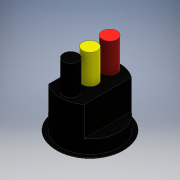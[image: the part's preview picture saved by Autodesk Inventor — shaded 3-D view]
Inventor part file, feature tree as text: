
AUTODESK INVENTOR PART (.ipt)
format: ipt  version: 2016 (Build 200138000, 138)  size: 154,112 bytes
history: native  units: mm
features: extrude x4, sketch x4, fillet x1, projected_geometry x1
ambient origin geometry x8: Origin, YZ Plane, XZ Plane, XY Plane, X Axis, Y Axis, Z Axis, Center Point
bodies: Solid1 (feature_tree)
feature tree (10):
  extrude  "Extrusion1"  Depth=4.5mm TaperAngle=0.0deg
  extrude  "Extrusion2"  Depth=10.0mm TaperAngle=0.0deg
  extrude  "Extrusion3"  Depth=1.0mm TaperAngle=0.0deg
  fillet  "Fillet1"  Radius=2.0mm
  extrude  "Extrusion4"  Depth=10.0mm
  sketch  "Sketch1"  dims[d0=20.0mm d1=4.5mm d2=0.0mm]
  sketch  "Sketch2"  dims[d3=12.0mm d4=10.0mm d5=0.0mm]
  projected_geometry  "Projected Loop1"
  sketch  "Sketch3"  dims[d6=23.0mm d7=1.0mm d8=0.0mm d9=2.0mm]
  sketch  "Sketch4"  dims[d10=5.0mm d11=5.0mm d12=5.0mm d13=10.0mm d14=0.0mm]
